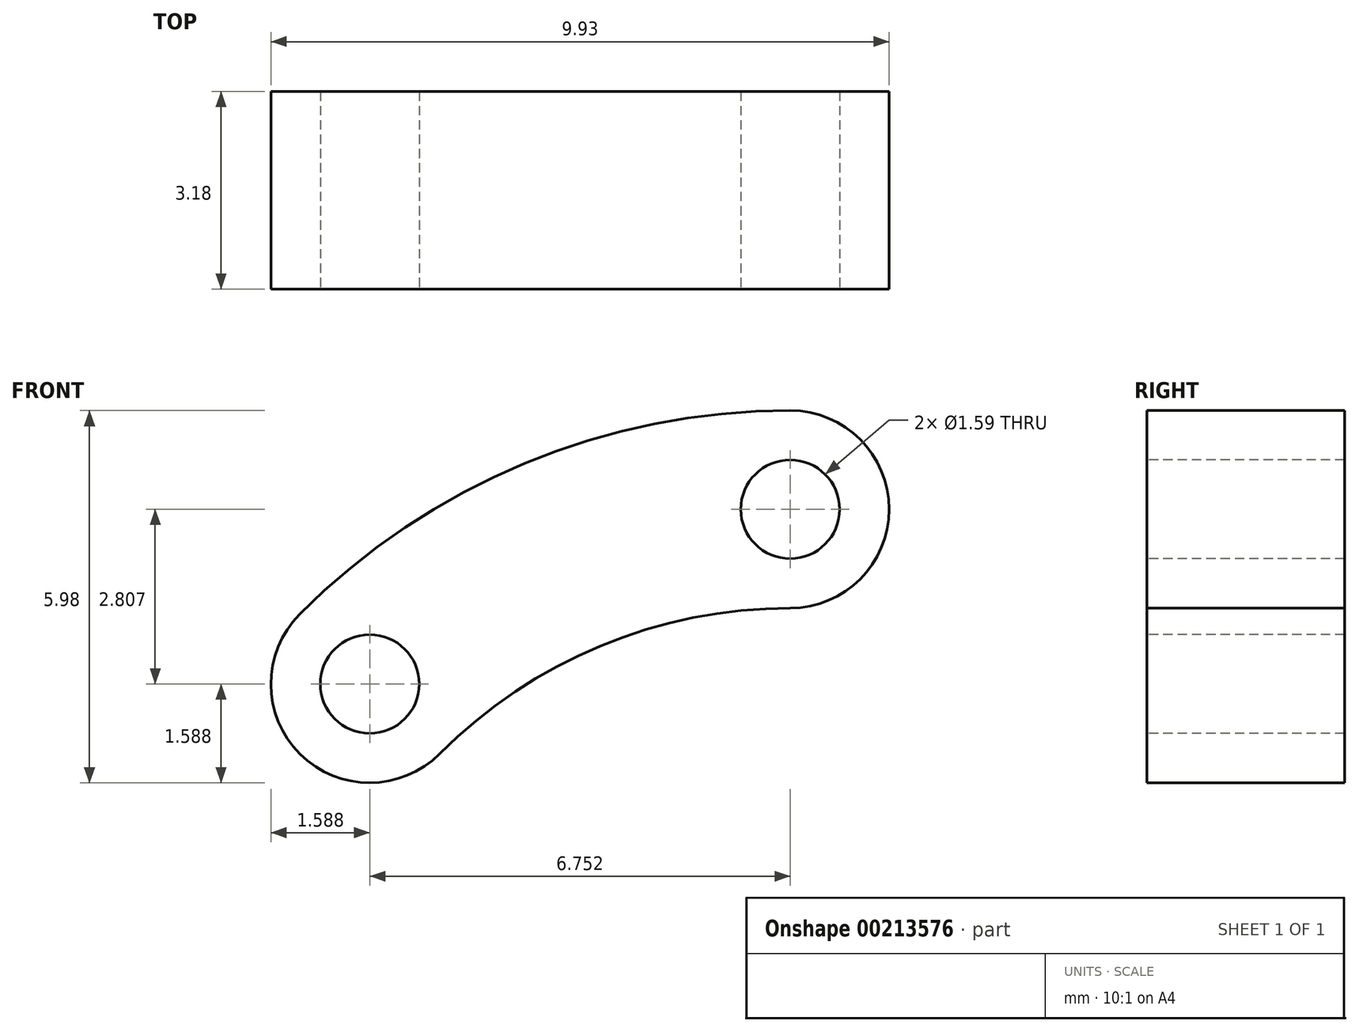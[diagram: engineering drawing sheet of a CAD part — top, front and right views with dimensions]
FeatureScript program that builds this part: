
annotation { "Feature Type Name" : "Feature", "Feature Type Description" : "" }
export const myFeature = defineFeature(function(context is Context, id is Id, definition is map)
    precondition{}
    {
        {
            var Q0;
            Q0=qCreatedBy(makeId("Front.planeOp"),FACE);
            var sketch = newSketch(context, id + "F0", { "sketchPlane" : qUnion([Q0])});
            skCircle(sketch, "E0", {"center": v(0, 0) * mm, "radius": 7.94 * mm});
            skCircle(sketch, "E1", {"center": v(0, 0) * mm, "radius": 11.11 * mm});
            skLineSegment(sketch, "E2", {"start": v(0, 15.6) * mm, "end": v(0, -17.37) * mm, "construction": true});
            skLineSegment(sketch, "E3", {"start": v(-14.41, 0) * mm, "end": v(15.98, 0) * mm, "construction": true});
            skCircle(sketch, "E4", {"center": v(0, 0) * mm, "radius": 9.53 * mm, "construction": true});
            skLineSegment(sketch, "E5", {"start": v(0, 0) * mm, "end": v(-11, 10.94) * mm, "construction": true});
            skLineSegment(sketch, "E6", {"start": v(0, 0) * mm, "end": v(-10.83, -10.88) * mm, "construction": true});
            skLineSegment(sketch, "E7", {"start": v(0, 0) * mm, "end": v(9.99, -9.94) * mm, "construction": true});
            skLineSegment(sketch, "E8", {"start": v(0, 0) * mm, "end": v(9.56, 9.6) * mm, "construction": true});
            skCircle(sketch, "E9", {"center": v(0, 9.53) * mm, "radius": 0.8 * mm});
            skCircle(sketch, "E10", {"center": v(-6.75, 6.72) * mm, "radius": 0.8 * mm});
            skCircle(sketch, "E11", {"center": v(-6.72, -6.75) * mm, "radius": 0.8 * mm});
            skCircle(sketch, "E12", {"center": v(0, -9.53) * mm, "radius": 0.8 * mm});
            skCircle(sketch, "E13", {"center": v(0, 9.53) * mm, "radius": 1.59 * mm});
            skCircle(sketch, "E14", {"center": v(-6.75, 6.72) * mm, "radius": 1.59 * mm});
            skCircle(sketch, "E15", {"center": v(-6.72, -6.75) * mm, "radius": 1.59 * mm});
            skCircle(sketch, "E16", {"center": v(0, -9.53) * mm, "radius": 1.59 * mm});
            skSolve(sketch);
        }
        {
            var Q0;
            {var subQ0=sQuery(id+"F0.wireOp",EDGE,"E14");var subQ1=sQuery(id+"F0.wireOp",EDGE,"E0");var subQ2=makeQuery(id+"F0.imprint","INTERSECT",VERTEX,{"derivedFrom":[subQ1,subQ0]});Q0=makeQuery(id+"F0.imprint","IMPRINT",FACE,{"disambiguationData":[TD([[makeQuery(id+"F0.imprint","IMPRINT",EDGE,{"disambiguationData":[TD([[subQ2,1.0]])],"derivedFrom":subQ1}),-1.0]])]});}
            var Q1;
            Q1=makeQuery(id+"F0.imprint","IMPRINT",FACE,{"disambiguationData":[TD([[makeQuery(id+"F0.imprint","IMPRINT",EDGE,{"derivedFrom":sQuery(id+"F0.wireOp",EDGE,"E9")}),-1.0]])]});
            var Q2;
            Q2=makeQuery(id+"F0.imprint","IMPRINT",FACE,{"disambiguationData":[TD([[makeQuery(id+"F0.imprint","IMPRINT",EDGE,{"derivedFrom":sQuery(id+"F0.wireOp",EDGE,"E10")}),-1.0]])]});
            extrude(context, id + "F1", {"entities" : qUnion([Q0, Q1, Q2]), "oppositeDirection" : true, "depth" : 3.17 * mm});
        }
    });
